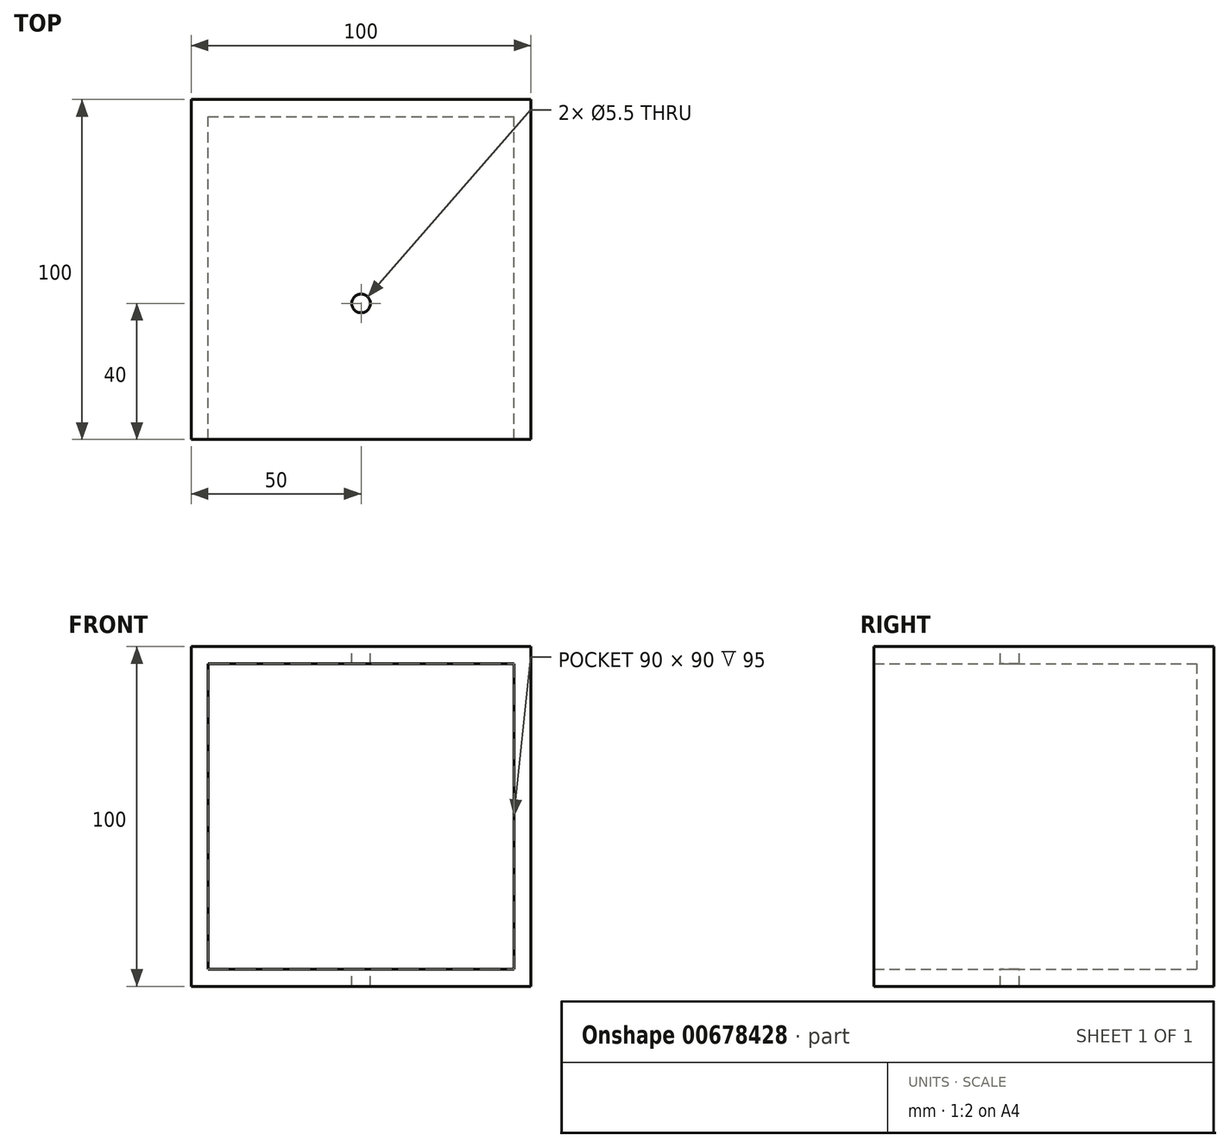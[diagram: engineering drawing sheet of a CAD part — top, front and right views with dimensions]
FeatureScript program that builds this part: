
annotation { "Feature Type Name" : "Feature", "Feature Type Description" : "" }
export const myFeature = defineFeature(function(context is Context, id is Id, definition is map)
    precondition{}
    {
        {
            var Q0;
            Q0=qCreatedBy(makeId("Top.planeOp"),FACE);
            var sketch = newSketch(context, id + "F0", { "sketchPlane" : qUnion([Q0])});
            skLineSegment(sketch, "E0.bottom", {"start": v(-50, -50) * mm, "end": v(50, -50) * mm});
            skLineSegment(sketch, "E0.top", {"start": v(-50, 50) * mm, "end": v(50, 50) * mm});
            skLineSegment(sketch, "E0.left", {"start": v(-50, -50) * mm, "end": v(-50, 50) * mm});
            skLineSegment(sketch, "E0.right", {"start": v(50, -50) * mm, "end": v(50, 50) * mm});
            skLineSegment(sketch, "E1.bottom", {"start": v(50, -50) * mm, "end": v(50, -50) * mm});
            skLineSegment(sketch, "E1.top", {"start": v(50, -50) * mm, "end": v(50, -50) * mm});
            skLineSegment(sketch, "E1.left", {"start": v(50, -50) * mm, "end": v(50, -50) * mm});
            skLineSegment(sketch, "E1.right", {"start": v(50, -50) * mm, "end": v(50, -50) * mm});
            skSolve(sketch);
        }
        {
            var Q0;
            Q0=makeQuery(id+"F0.imprint","IMPRINT",FACE,{"disambiguationData":[TD([[makeQuery(id+"F0.imprint","IMPRINT",EDGE,{"derivedFrom":sQuery(id+"F0.wireOp",EDGE,"E0.bottom")}),1.0]])]});
            extrude(context, id + "F1", {"entities" : qUnion([Q0]), "depth" : 100 * mm, "offsetDistance" : 25 * mm});
        }
        {
            var Q0;
            Q0=makeQuery(id+"F1.opExtrude","SWEPT_FACE",FACE,{"disambiguationData":[OSD([sQuery(id+"F0.wireOp",EDGE,"E0.bottom")])]});
            shell(context, id + "F2", {"entities" : qUnion([Q0]), "thickness" : 5 * mm});
        }
        {
            var Q0;
            Q0=makeQuery(id+"F1.opExtrude","CAP_FACE",FACE,{"disambiguationData":[OSD([sQuery(id+"F0.wireOp",EDGE,"E0.bottom"),sQuery(id+"F0.wireOp",EDGE,"E0.top"),sQuery(id+"F0.wireOp",EDGE,"E0.left"),sQuery(id+"F0.wireOp",EDGE,"E0.right")])],"isStart":false});
            var sketch = newSketch(context, id + "F3", { "sketchPlane" : qUnion([Q0])});
            skPoint(sketch, "E2", {"position": v(0, -10) * mm});
            skSolve(sketch);
        }
        {
            var Q0;
            Q0=sQuery(id+"F3.wireOp",VERTEX,"E2");
            var Q1;
            Q1=makeQuery(id+"F1.opExtrude","SWEPT_BODY",BODY,{"disambiguationData":[OSD([sQuery(id+"F0.wireOp",EDGE,"E0.bottom"),sQuery(id+"F0.wireOp",EDGE,"E0.top"),sQuery(id+"F0.wireOp",EDGE,"E0.left"),sQuery(id+"F0.wireOp",EDGE,"E0.right")])]});
            hole(context, id + "F4", {"style" : HoleStyle.SIMPLE, "endStyle" : HoleEndStyle.THROUGH, "standardTappedOrClearance" : lookupTablePath({ "fit" : "Normal", "standard" : "ISO", "size" : "M5", "type" : "Clearance" }), "standardBlindInLast" : lookupTablePath({ "fit" : "Standard", "standard" : "ISO", "size" : "M5", "type" : "Clearance" }), "holeDiameter" : 5.5 * mm, "majorDiameter" : 5 * mm, "isTappedThrough" : true, "tappedDepth" : 12 * mm, "tapClearance" : 3, "locations" : qUnion([Q0]), "scope" : qUnion([Q1])});
        }
    });
